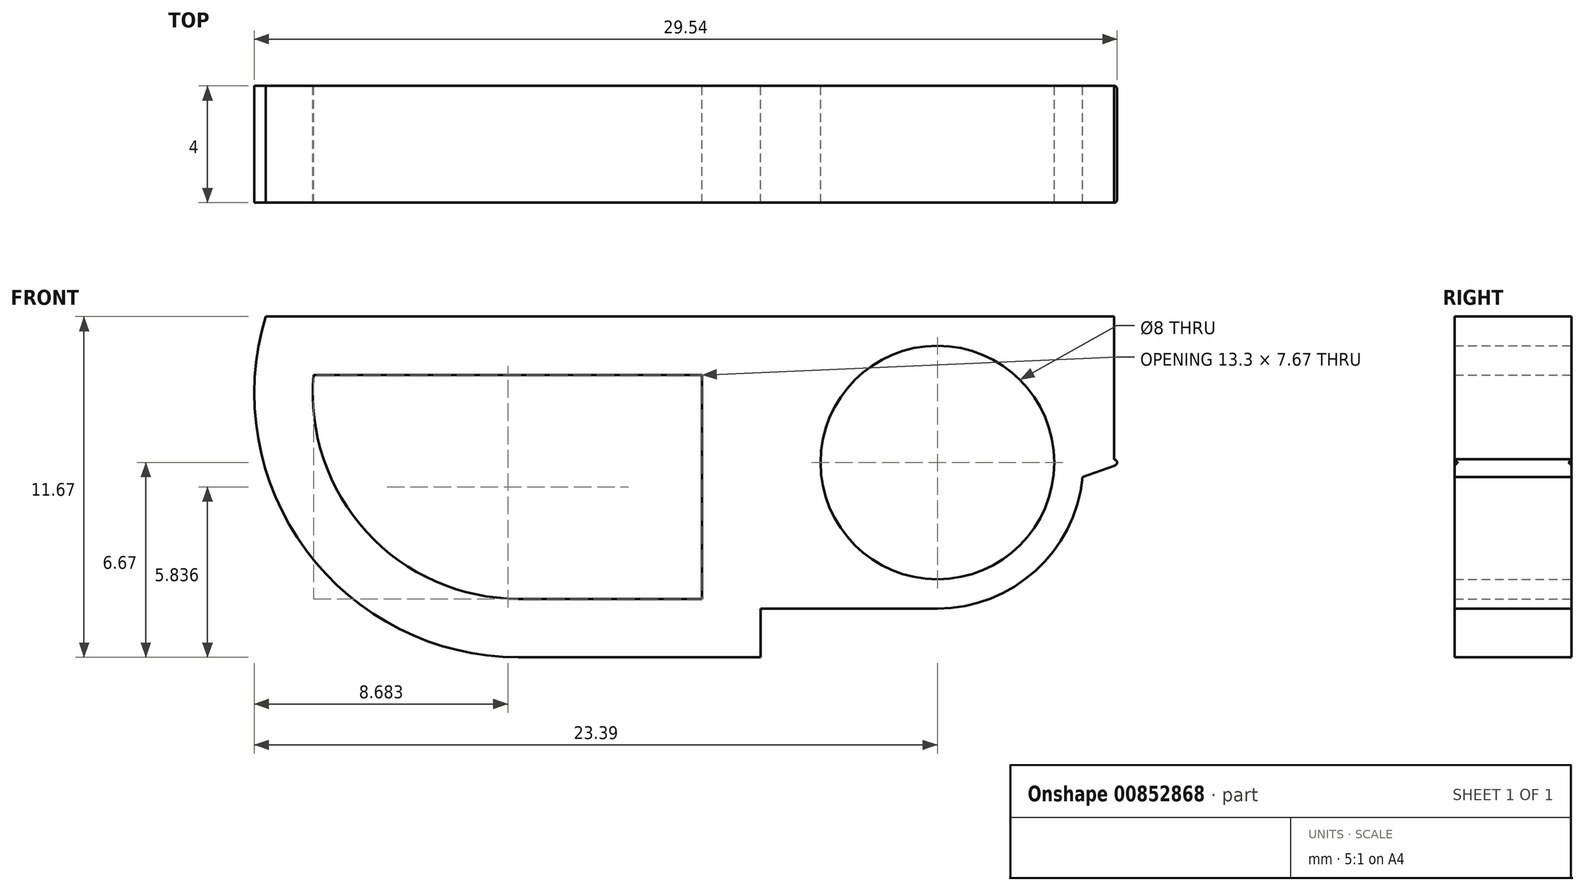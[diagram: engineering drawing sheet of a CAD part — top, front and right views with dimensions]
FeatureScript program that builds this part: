
annotation { "Feature Type Name" : "Feature", "Feature Type Description" : "" }
export const myFeature = defineFeature(function(context is Context, id is Id, definition is map)
    precondition{}
    {
        {
            var Q0;
            Q0=qCreatedBy(makeId("Front.planeOp"),FACE);
            var sketch = newSketch(context, id + "F0", { "sketchPlane" : qUnion([Q0])});
            skCircle(sketch, "E0", {"center": v(0, 0) * mm, "radius": 4 * mm});
            skArc(sketch, "E1", {"start": v(0, -5) * mm, "mid": v(5, 0) * mm, "end": v(0, 5) * mm});
            skLineSegment(sketch, "E2", {"start": v(0, -5) * mm, "end": v(-6.05, -5) * mm});
            skLineSegment(sketch, "E3", {"start": v(0, 5) * mm, "end": v(-6.05, 5) * mm});
            skLineSegment(sketch, "E4", {"start": v(-6.05, 5) * mm, "end": v(-6.05, -5) * mm});
            skSolve(sketch);
        }
        {
            var Q0;
            Q0 = qSketchRegion(id + "F0", true);
            extrude(context, id + "F1", {"entities" : qUnion([Q0]), "depth" : 4 * mm, "offsetDistance" : 25 * mm});
        }
        {
            var Q0;
            Q0=qCreatedBy(makeId("Front.planeOp"),FACE);
            var sketch = newSketch(context, id + "F2", { "sketchPlane" : qUnion([Q0])});
            skLineSegment(sketch, "E5", {"start": v(6.35, 0) * mm, "end": v(4.97, 0.5) * mm});
            skPoint(sketch, "E5.startSnap0", {"position": v(5, 0) * mm});
            skLineSegment(sketch, "E6.MirrorCS", {"start": v(6.35, 0) * mm, "end": v(4.97, -0.5) * mm});
            skLineSegment(sketch, "E7", {"start": v(4.97, 0.5) * mm, "end": v(4.97, -0.5) * mm});
            skLineSegment(sketch, "E8", {"start": v(4.97, 0) * mm, "end": v(6.46, 0) * mm, "construction": true});
            skLineSegment(sketch, "E9", {"start": v(6.15, 0.07) * mm, "end": v(6.15, -0.07) * mm});
            skSolve(sketch);
        }
        {
            var Q0;
            {var subQ0=sQuery(id+"F2.wireOp",EDGE,"E7");Q0=makeQuery(id+"F2.imprint","IMPRINT",FACE,{"disambiguationData":[TD([[makeQuery(id+"F2.imprint","IMPRINT",EDGE,{"derivedFrom":subQ0}),1.0]])]});}
            var Q1;
            Q1=makeQuery(id+"F1.opExtrude","CAP_FACE",FACE,{"disambiguationData":[OSD([sQuery(id+"F0.wireOp",EDGE,"E0"),sQuery(id+"F0.wireOp",EDGE,"E1"),sQuery(id+"F0.wireOp",EDGE,"E2"),sQuery(id+"F0.wireOp",EDGE,"E3"),sQuery(id+"F0.wireOp",EDGE,"E4")])],"isStart":false});
            extrude(context, id + "F3", {"entities" : qUnion([Q0]), "operationType" : NewBodyOperationType.ADD, "endBound" : BoundingType.UP_TO_SURFACE, "depth" : 25 * mm, "endBoundEntityFace" : qUnion([Q1]), "offsetDistance" : 25 * mm});
        }
        {
            var Q0;
            Q0=makeQuery(id+"F3.opExtrude","SWEPT_FACE",FACE,{"disambiguationData":[OSD([sQuery(id+"F2.wireOp",EDGE,"E9")])]});
            fillet(context, id + "F4", {"entities" : qUnion([Q0]), "radius" : .1 * mm, "tangentPropagation" : true, "allowEdgeOverflow" : false});
        }
        {
            var Q0;
            Q0=qCreatedBy(makeId("Front.planeOp"),FACE);
            var sketch = newSketch(context, id + "F5", { "sketchPlane" : qUnion([Q0])});
            skLineSegment(sketch, "E10.0", {"start": v(-6.05, 5) * mm, "end": v(-6.05, -5) * mm});
            skLineSegment(sketch, "E11", {"start": v(-6.05, 5) * mm, "end": v(-23, 5) * mm});
            skLineSegment(sketch, "E12", {"start": v(-6.05, -6.67) * mm, "end": v(-14.35, -6.67) * mm});
            skArc(sketch, "E13", {"start": v(-14.35, -6.67) * mm, "mid": v(-21.6, -3.01) * mm, "end": v(-23, 5) * mm});
            skLineSegment(sketch, "E14", {"start": v(-6.05, -6.67) * mm, "end": v(-6.05, -5) * mm});
            skLineSegment(sketch, "E15.0", {"start": v(-8.05, 3) * mm, "end": v(-21.36, 3) * mm});
            skLineSegment(sketch, "E15.1", {"start": v(-8.05, 3) * mm, "end": v(-8.05, -4.67) * mm});
            skLineSegment(sketch, "E15.2", {"start": v(-8.05, -4.67) * mm, "end": v(-14.35, -4.67) * mm});
            skArc(sketch, "E15.3", {"start": v(-14.35, -4.67) * mm, "mid": v(-19.54, -2.38) * mm, "end": v(-21.36, 3) * mm});
            skSolve(sketch);
        }
        {
            var Q0;
            Q0=makeQuery(id+"F5.imprint","IMPRINT",FACE,{"disambiguationData":[TD([[makeQuery(id+"F5.imprint","IMPRINT",EDGE,{"derivedFrom":sQuery(id+"F5.wireOp",EDGE,"E10.0")}),-1.0]])]});
            var Q1;
            {var subQ0=sQuery(id+"F0.wireOp",EDGE,"E4");var subQ1=sQuery(id+"F0.wireOp",EDGE,"E3");var subQ2=sQuery(id+"F0.wireOp",EDGE,"E2");var subQ3=sQuery(id+"F0.wireOp",EDGE,"E1");var subQ4=sQuery(id+"F0.wireOp",EDGE,"E0");Q1=makeQuery(id+"FEm3DrMPeMO6d6I_1.7.F3.boolean.opBoolean","MERGE",FACE,{"derivedFrom":[makeQuery(id+"FEm3DrMPeMO6d6I_1.6.F3.boolean.opBoolean","MERGE",FACE,{"derivedFrom":[makeQuery(id+"FEm3DrMPeMO6d6I_1.5.F3.boolean.opBoolean","MERGE",FACE,{"derivedFrom":[makeQuery(id+"FEm3DrMPeMO6d6I_1.4.F3.boolean.opBoolean","MERGE",FACE,{"derivedFrom":[makeQuery(id+"FEm3DrMPeMO6d6I_1.3.F3.boolean.opBoolean","MERGE",FACE,{"derivedFrom":[makeQuery(id+"FEm3DrMPeMO6d6I_1.2.F3.boolean.opBoolean","MERGE",FACE,{"derivedFrom":[makeQuery(id+"FEm3DrMPeMO6d6I_1.1.F3.boolean.opBoolean","MERGE",FACE,{"derivedFrom":[makeQuery(id+"F3.boolean.opBoolean","MERGE",FACE,{"derivedFrom":[makeQuery(id+"F1.opExtrude","CAP_FACE",FACE,{"disambiguationData":[OSD([subQ4,subQ3,subQ2,subQ1,subQ0])],"isStart":false}),makeQuery(id+"F3.opExtrude","CAP_FACE",FACE,{"disambiguationData":[OSD([subQ4,subQ3,subQ2,subQ1,subQ0])],"isStart":false})]}),makeQuery(id+"FEm3DrMPeMO6d6I_1.1.F3.opExtrude","CAP_FACE",FACE,{"disambiguationData":[OSD([subQ4,subQ3,subQ2,subQ1,subQ0])],"isStart":false})]}),makeQuery(id+"FEm3DrMPeMO6d6I_1.2.F3.opExtrude","CAP_FACE",FACE,{"disambiguationData":[OSD([subQ4,subQ3,subQ2,subQ1,subQ0])],"isStart":false})]}),makeQuery(id+"FEm3DrMPeMO6d6I_1.3.F3.opExtrude","CAP_FACE",FACE,{"disambiguationData":[OSD([subQ4,subQ3,subQ2,subQ1,subQ0])],"isStart":false})]}),makeQuery(id+"FEm3DrMPeMO6d6I_1.4.F3.opExtrude","CAP_FACE",FACE,{"disambiguationData":[OSD([subQ4,subQ3,subQ2,subQ1,subQ0])],"isStart":false})]}),makeQuery(id+"FEm3DrMPeMO6d6I_1.5.F3.opExtrude","CAP_FACE",FACE,{"disambiguationData":[OSD([subQ4,subQ3,subQ2,subQ1,subQ0])],"isStart":false})]}),makeQuery(id+"FEm3DrMPeMO6d6I_1.6.F3.opExtrude","CAP_FACE",FACE,{"disambiguationData":[OSD([subQ4,subQ3,subQ2,subQ1,subQ0])],"isStart":false})]}),makeQuery(id+"FEm3DrMPeMO6d6I_1.7.F3.opExtrude","CAP_FACE",FACE,{"disambiguationData":[OSD([subQ4,subQ3,subQ2,subQ1,subQ0])],"isStart":false})]});}
            extrude(context, id + "F6", {"entities" : qUnion([Q0]), "operationType" : NewBodyOperationType.ADD, "endBound" : BoundingType.UP_TO_SURFACE, "depth" : 25 * mm, "endBoundEntityFace" : qUnion([Q1]), "offsetDistance" : 25 * mm});
        }
        {
            var Q0;
            Q0=qCreatedBy(makeId("Front.planeOp"),FACE);
            var sketch = newSketch(context, id + "F7", { "sketchPlane" : qUnion([Q0])});
            skArc(sketch, "E16.0", {"start": v(4.97, 0.5) * mm, "mid": v(3.35, 3.7) * mm, "end": v(0, 5) * mm});
            skLineSegment(sketch, "E17", {"start": v(6.05, 5) * mm, "end": v(0, 5) * mm});
            skLineSegment(sketch, "E18.0", {"start": v(6.05, 0.1) * mm, "end": v(4.97, 0.5) * mm});
            skLineSegment(sketch, "E19", {"start": v(6.05, 0.1) * mm, "end": v(6.05, 5) * mm});
            skSolve(sketch);
        }
        {
            var Q0;
            Q0 = qSketchRegion(id + "F7", true);
            var Q1;
            {var subQ0=sQuery(id+"F0.wireOp",EDGE,"E4");var subQ1=sQuery(id+"F0.wireOp",EDGE,"E3");var subQ2=sQuery(id+"F0.wireOp",EDGE,"E2");var subQ3=sQuery(id+"F0.wireOp",EDGE,"E1");var subQ4=sQuery(id+"F0.wireOp",EDGE,"E0");Q1=makeQuery(id+"F6.boolean.opBoolean","MERGE",FACE,{"derivedFrom":[makeQuery(id+"FEm3DrMPeMO6d6I_1.7.F3.boolean.opBoolean","MERGE",FACE,{"derivedFrom":[makeQuery(id+"FEm3DrMPeMO6d6I_1.6.F3.boolean.opBoolean","MERGE",FACE,{"derivedFrom":[makeQuery(id+"FEm3DrMPeMO6d6I_1.5.F3.boolean.opBoolean","MERGE",FACE,{"derivedFrom":[makeQuery(id+"FEm3DrMPeMO6d6I_1.4.F3.boolean.opBoolean","MERGE",FACE,{"derivedFrom":[makeQuery(id+"FEm3DrMPeMO6d6I_1.3.F3.boolean.opBoolean","MERGE",FACE,{"derivedFrom":[makeQuery(id+"FEm3DrMPeMO6d6I_1.2.F3.boolean.opBoolean","MERGE",FACE,{"derivedFrom":[makeQuery(id+"FEm3DrMPeMO6d6I_1.1.F3.boolean.opBoolean","MERGE",FACE,{"derivedFrom":[makeQuery(id+"F3.boolean.opBoolean","MERGE",FACE,{"derivedFrom":[makeQuery(id+"F1.opExtrude","CAP_FACE",FACE,{"disambiguationData":[OSD([subQ4,subQ3,subQ2,subQ1,subQ0])],"isStart":false}),makeQuery(id+"F3.opExtrude","CAP_FACE",FACE,{"disambiguationData":[OSD([subQ4,subQ3,subQ2,subQ1,subQ0])],"isStart":false})]}),makeQuery(id+"FEm3DrMPeMO6d6I_1.1.F3.opExtrude","CAP_FACE",FACE,{"disambiguationData":[OSD([subQ4,subQ3,subQ2,subQ1,subQ0])],"isStart":false})]}),makeQuery(id+"FEm3DrMPeMO6d6I_1.2.F3.opExtrude","CAP_FACE",FACE,{"disambiguationData":[OSD([subQ4,subQ3,subQ2,subQ1,subQ0])],"isStart":false})]}),makeQuery(id+"FEm3DrMPeMO6d6I_1.3.F3.opExtrude","CAP_FACE",FACE,{"disambiguationData":[OSD([subQ4,subQ3,subQ2,subQ1,subQ0])],"isStart":false})]}),makeQuery(id+"FEm3DrMPeMO6d6I_1.4.F3.opExtrude","CAP_FACE",FACE,{"disambiguationData":[OSD([subQ4,subQ3,subQ2,subQ1,subQ0])],"isStart":false})]}),makeQuery(id+"FEm3DrMPeMO6d6I_1.5.F3.opExtrude","CAP_FACE",FACE,{"disambiguationData":[OSD([subQ4,subQ3,subQ2,subQ1,subQ0])],"isStart":false})]}),makeQuery(id+"FEm3DrMPeMO6d6I_1.6.F3.opExtrude","CAP_FACE",FACE,{"disambiguationData":[OSD([subQ4,subQ3,subQ2,subQ1,subQ0])],"isStart":false})]}),makeQuery(id+"FEm3DrMPeMO6d6I_1.7.F3.opExtrude","CAP_FACE",FACE,{"disambiguationData":[OSD([subQ4,subQ3,subQ2,subQ1,subQ0])],"isStart":false})]}),makeQuery(id+"F6.opExtrude","CAP_FACE",FACE,{"disambiguationData":[OSD([subQ4,subQ3,subQ2,subQ1,subQ0])],"isStart":false})]});}
            extrude(context, id + "F8", {"entities" : qUnion([Q0]), "operationType" : NewBodyOperationType.ADD, "endBound" : BoundingType.UP_TO_SURFACE, "depth" : 25 * mm, "endBoundEntityFace" : qUnion([Q1]), "offsetDistance" : 25 * mm});
        }
    });
